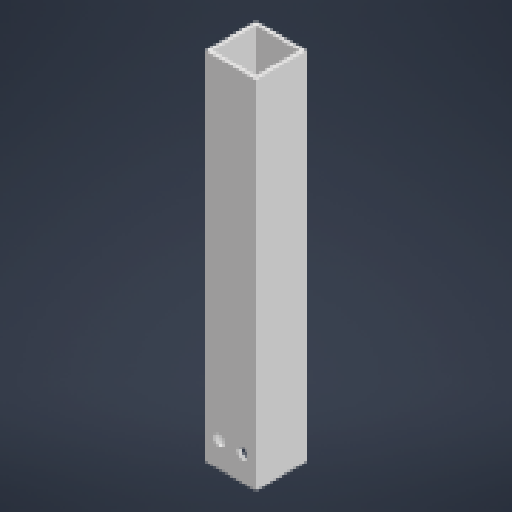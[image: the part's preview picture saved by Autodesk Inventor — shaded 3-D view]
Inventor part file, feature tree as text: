
AUTODESK INVENTOR PART (.ipt)
format: ipt  version: 2024 (Build 280153000, 153)  size: 154,112 bytes
history: native  units: mm
features: extrude x2, sketch x2, other x1
ambient origin geometry x8: Origin, YZ Plane, XZ Plane, XY Plane, X Axis, Y Axis, Z Axis, Center Point
bodies: Body1 (feature_tree)
feature tree (5):
  other  "Твердое тело1"
  extrude  "Выдавливание1"  Depth=20.0mm
  extrude  "Выдавливание2"  Depth=1.5mm
  sketch  "Эскиз1"
  sketch  "Эскиз2"
